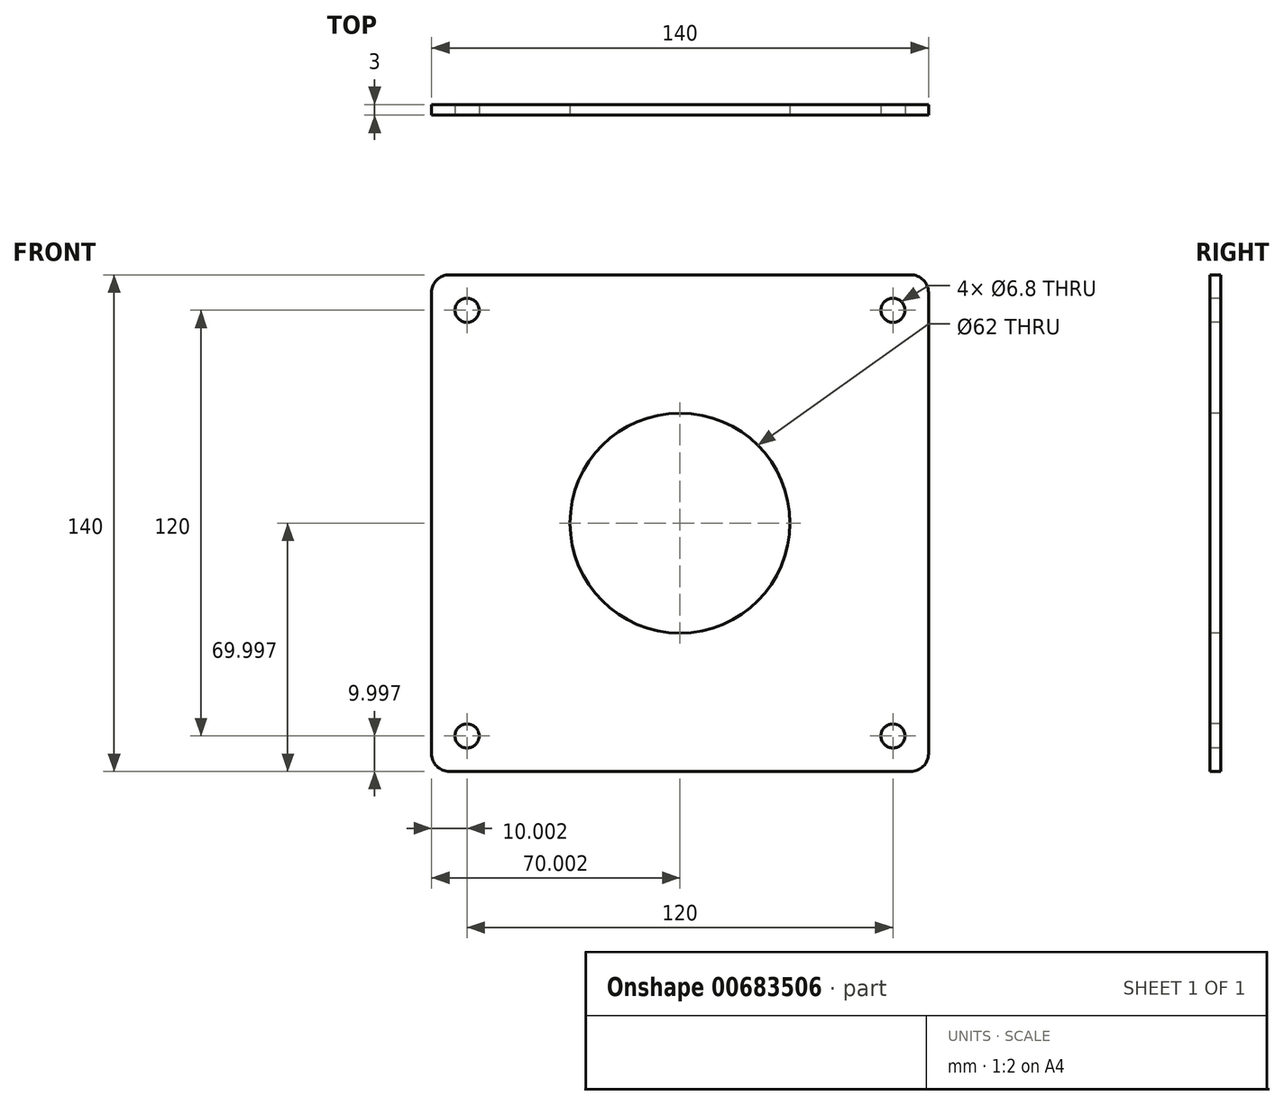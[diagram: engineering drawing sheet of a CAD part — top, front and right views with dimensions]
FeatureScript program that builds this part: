
annotation { "Feature Type Name" : "Feature", "Feature Type Description" : "" }
export const myFeature = defineFeature(function(context is Context, id is Id, definition is map)
    precondition{}
    {
        {
            var Q0;
            Q0=qCreatedBy(makeId("Front.planeOp"),FACE);
            var sketch = newSketch(context, id + "F0", { "sketchPlane" : qUnion([Q0])});
            skLineSegment(sketch, "E0.bottom", {"start": v(-1776.2, -1439.16) * mm, "end": v(-1636.2, -1439.16) * mm});
            skLineSegment(sketch, "E0.top", {"start": v(-1776.2, -1579.16) * mm, "end": v(-1636.2, -1579.16) * mm});
            skLineSegment(sketch, "E0.left", {"start": v(-1776.2, -1439.16) * mm, "end": v(-1776.2, -1579.16) * mm});
            skLineSegment(sketch, "E0.right", {"start": v(-1636.2, -1439.16) * mm, "end": v(-1636.2, -1579.16) * mm});
            skPoint(sketch, "E1", {"position": v(-1766.2, -1449.16) * mm});
            skPoint(sketch, "E2", {"position": v(-1646.2, -1449.16) * mm});
            skPoint(sketch, "E3", {"position": v(-1646.2, -1569.16) * mm});
            skPoint(sketch, "E4", {"position": v(-1766.2, -1569.16) * mm});
            skSolve(sketch);
        }
        {
            var Q0;
            Q0 = qSketchRegion(id + "F0", true);
            extrude(context, id + "F1", {"entities" : qUnion([Q0]), "depth" : 3 * mm, "offsetDistance" : 25 * mm});
        }
        {
            var Q0;
            Q0=makeQuery(id+"F1.opExtrude","CAP_FACE",FACE,{"disambiguationData":[OSD([sQuery(id+"F0.wireOp",EDGE,"E0.bottom"),sQuery(id+"F0.wireOp",EDGE,"E0.top"),sQuery(id+"F0.wireOp",EDGE,"E0.left"),sQuery(id+"F0.wireOp",EDGE,"E0.right")])],"isStart":false});
            var sketch = newSketch(context, id + "F2", { "sketchPlane" : qUnion([Q0])});
            skPoint(sketch, "E5", {"position": v(-1766.2, -1449.16) * mm});
            skPoint(sketch, "E6", {"position": v(-1646.2, -1449.16) * mm});
            skPoint(sketch, "E7", {"position": v(-1646.2, -1569.16) * mm});
            skPoint(sketch, "E8", {"position": v(-1766.2, -1569.16) * mm});
            skSolve(sketch);
        }
        {
            var Q0;
            Q0=sQuery(id+"F2.wireOp",VERTEX,"E5");
            var Q1;
            Q1=sQuery(id+"F2.wireOp",VERTEX,"E6");
            var Q2;
            Q2=sQuery(id+"F2.wireOp",VERTEX,"E7");
            var Q3;
            Q3=sQuery(id+"F2.wireOp",VERTEX,"E8");
            var Q4;
            Q4=makeQuery(id+"F1.opExtrude","SWEPT_BODY",BODY,{"disambiguationData":[OSD([sQuery(id+"F0.wireOp",EDGE,"E0.bottom"),sQuery(id+"F0.wireOp",EDGE,"E0.top"),sQuery(id+"F0.wireOp",EDGE,"E0.left"),sQuery(id+"F0.wireOp",EDGE,"E0.right")])]});
            hole(context, id + "F3", {"style" : HoleStyle.SIMPLE, "endStyle" : HoleEndStyle.BLIND, "holeDiameter" : 6.8 * mm, "majorDiameter" : 5 * mm, "holeDepth" : 10 * mm, "isTappedThrough" : true, "tappedDepth" : 12 * mm, "tapClearance" : 3, "locations" : qUnion([Q0, Q1, Q2, Q3]), "scope" : qUnion([Q4])});
        }
        {
            var Q0;
            Q0=makeQuery(id+"F1.opExtrude","SWEPT_EDGE",EDGE,{"disambiguationData":[OSD([sQuery(id+"F0.wireOp",EDGE,"E0.bottom"),sQuery(id+"F0.wireOp",EDGE,"E0.right")])]});
            var Q1;
            Q1=makeQuery(id+"F1.opExtrude","SWEPT_EDGE",EDGE,{"disambiguationData":[OSD([sQuery(id+"F0.wireOp",EDGE,"E0.top"),sQuery(id+"F0.wireOp",EDGE,"E0.right")])]});
            var Q2;
            Q2=makeQuery(id+"F1.opExtrude","SWEPT_EDGE",EDGE,{"disambiguationData":[OSD([sQuery(id+"F0.wireOp",EDGE,"E0.bottom"),sQuery(id+"F0.wireOp",EDGE,"E0.left")])]});
            var Q3;
            Q3=makeQuery(id+"F1.opExtrude","SWEPT_EDGE",EDGE,{"disambiguationData":[OSD([sQuery(id+"F0.wireOp",EDGE,"E0.top"),sQuery(id+"F0.wireOp",EDGE,"E0.left")])]});
            fillet(context, id + "F4", {"entities" : qUnion([Q0, Q1, Q2, Q3]), "radius" : 5 * mm, "tangentPropagation" : true, "allowEdgeOverflow" : false});
        }
        {
            var Q0;
            Q0=makeQuery(id+"F1.opExtrude","CAP_FACE",FACE,{"disambiguationData":[OSD([sQuery(id+"F0.wireOp",EDGE,"E0.bottom"),sQuery(id+"F0.wireOp",EDGE,"E0.top"),sQuery(id+"F0.wireOp",EDGE,"E0.left"),sQuery(id+"F0.wireOp",EDGE,"E0.right")])],"isStart":false});
            var sketch = newSketch(context, id + "F5", { "sketchPlane" : qUnion([Q0])});
            skPoint(sketch, "E9", {"position": v(-1706.2, -1509.16) * mm});
            skSolve(sketch);
        }
        {
            var Q0;
            Q0=sQuery(id+"F5.wireOp",VERTEX,"E9");
            var Q1;
            Q1=makeQuery(id+"F1.opExtrude","SWEPT_BODY",BODY,{"disambiguationData":[OSD([sQuery(id+"F0.wireOp",EDGE,"E0.bottom"),sQuery(id+"F0.wireOp",EDGE,"E0.top"),sQuery(id+"F0.wireOp",EDGE,"E0.left"),sQuery(id+"F0.wireOp",EDGE,"E0.right")])]});
            hole(context, id + "F6", {"style" : HoleStyle.SIMPLE, "endStyle" : HoleEndStyle.BLIND, "holeDiameter" : 62 * mm, "majorDiameter" : 5 * mm, "holeDepth" : 10 * mm, "isTappedThrough" : true, "tappedDepth" : 12 * mm, "tapClearance" : 3, "locations" : qUnion([Q0]), "scope" : qUnion([Q1])});
        }
    });
